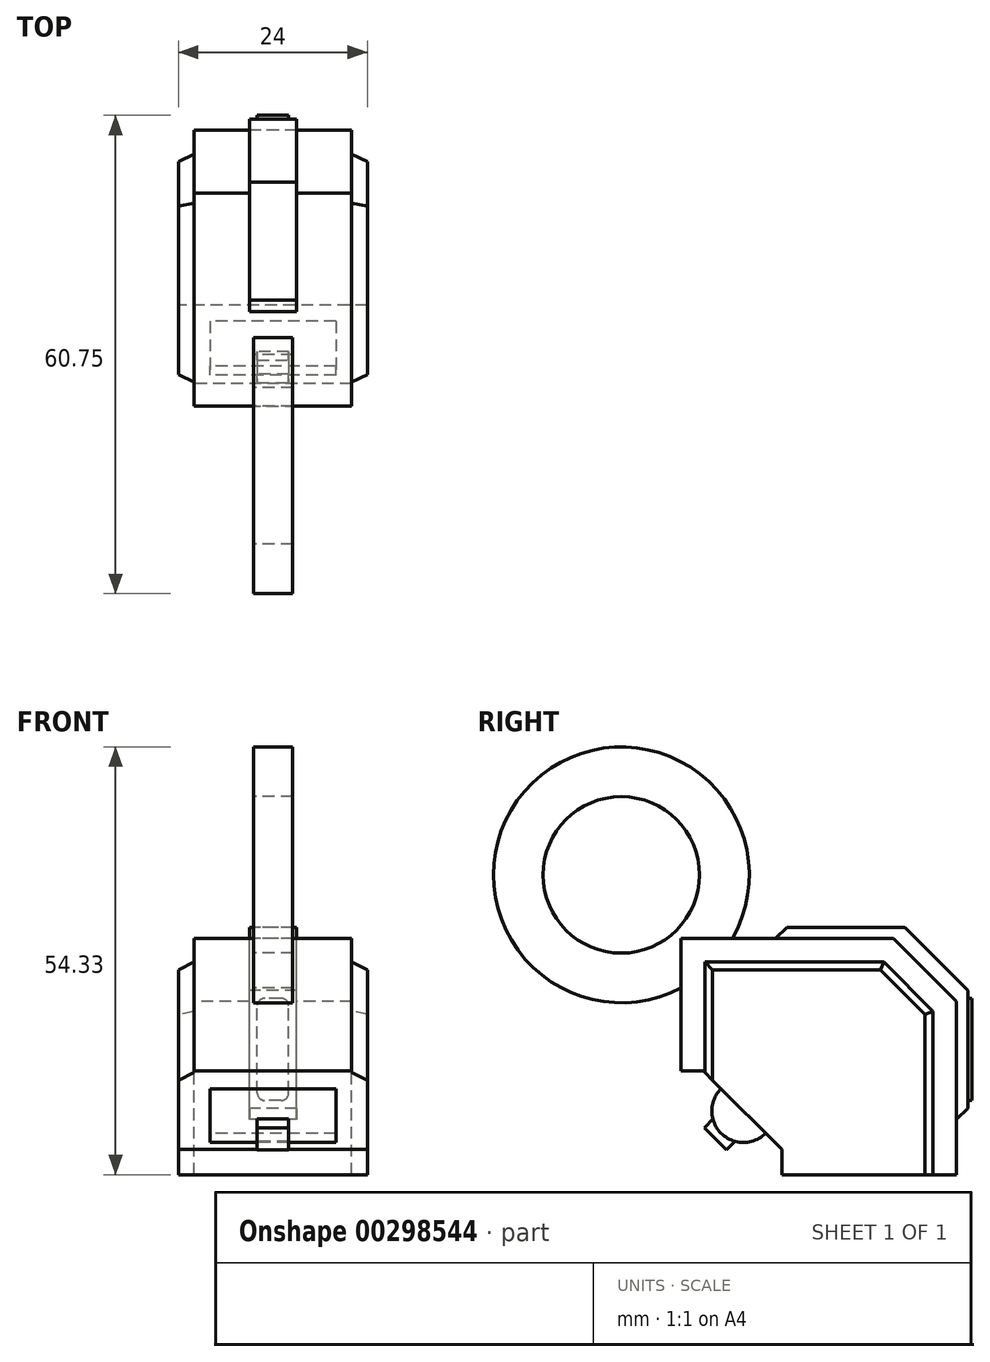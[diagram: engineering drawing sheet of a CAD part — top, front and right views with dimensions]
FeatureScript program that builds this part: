
annotation { "Feature Type Name" : "Feature", "Feature Type Description" : "" }
export const myFeature = defineFeature(function(context is Context, id is Id, definition is map)
    precondition{}
    {
        {
            var Q0;
            Q0=qCreatedBy(makeId("Right.planeOp"),FACE);
            cPlane(context, id + "F0", {"entities" : qUnion([Q0]), "cplaneType" : CPlaneType.OFFSET, "offset" : 10 * mm, "width" : 150 * mm, "height" : 150 * mm});
        }
        {
            var Q0;
            Q0=qCreatedBy(makeId("Right.planeOp"),FACE);
            var sketch = newSketch(context, id + "F1", { "sketchPlane" : qUnion([Q0])});
            skLineSegment(sketch, "E0.top", {"start": v(-35, 0) * mm, "end": v(0, 0) * mm});
            skLineSegment(sketch, "E0.left", {"start": v(-35, 30) * mm, "end": v(-35, 0) * mm});
            skLineSegment(sketch, "E1", {"start": v(0, 0) * mm, "end": v(0, 22) * mm});
            skLineSegment(sketch, "E2", {"start": v(-35, 30) * mm, "end": v(-8, 30) * mm});
            skLineSegment(sketch, "E3", {"start": v(-8, 30) * mm, "end": v(0, 22) * mm});
            skLineSegment(sketch, "E4.0", {"start": v(-32, 3) * mm, "end": v(-3, 3) * mm});
            skLineSegment(sketch, "E4.1", {"start": v(-32, 27) * mm, "end": v(-32, 3) * mm});
            skLineSegment(sketch, "E4.2", {"start": v(-3, 3) * mm, "end": v(-3, 20.76) * mm});
            skLineSegment(sketch, "E4.3", {"start": v(-9.24, 27) * mm, "end": v(-3, 20.76) * mm});
            skLineSegment(sketch, "E4.4", {"start": v(-32, 27) * mm, "end": v(-9.24, 27) * mm});
            skLineSegment(sketch, "E5.top", {"start": v(-3, 0) * mm, "end": v(-32, 0) * mm});
            skLineSegment(sketch, "E5.left", {"start": v(-3, 3) * mm, "end": v(-3, 0) * mm});
            skLineSegment(sketch, "E5.right", {"start": v(-32, 3) * mm, "end": v(-32, 0) * mm});
            skSolve(sketch);
        }
        {
            var Q0;
            Q0=makeQuery(id+"F1.imprint","IMPRINT",FACE,{"disambiguationData":[TD([[makeQuery(id+"F1.imprint","IMPRINT",EDGE,{"derivedFrom":sQuery(id+"F1.wireOp",EDGE,"E0.top")}),1.0]])]});
            extrude(context, id + "F2", {"entities" : qUnion([Q0]), "depth" : 20 * mm});
        }
        {
            var Q0;
            Q0=makeQuery(id+"F1.imprint","IMPRINT",FACE,{"disambiguationData":[TD([[makeQuery(id+"F1.imprint","IMPRINT",EDGE,{"derivedFrom":sQuery(id+"F1.wireOp",EDGE,"E4.0")}),1.0]])]});
            extrude(context, id + "F3", {"entities" : qUnion([Q0]), "operationType" : NewBodyOperationType.ADD, "depth" : 22 * mm, "hasSecondDirection" : true, "secondDirectionOppositeDirection" : true, "secondDirectionDepth" : 2 * mm});
        }
        {
            var Q0;
            Q0=makeQuery(id+"F2.opExtrude","SWEPT_FACE",FACE,{"disambiguationData":[OSD([sQuery(id+"F1.wireOp",EDGE,"E1")])]});
            var sketch = newSketch(context, id + "F4", { "sketchPlane" : qUnion([Q0])});
            skLineSegment(sketch, "E6", {"start": v(-13, 22) * mm, "end": v(-7, 22) * mm});
            skLineSegment(sketch, "E7.0", {"start": v(-13, 7) * mm, "end": v(-7, 7) * mm});
            skLineSegment(sketch, "E8", {"start": v(-13, 7) * mm, "end": v(-13, 22) * mm});
            skLineSegment(sketch, "E9", {"start": v(-7, 7) * mm, "end": v(-7, 22) * mm});
            skSolve(sketch);
        }
        {
            var Q0;
            Q0=makeQuery(id+"F2.opExtrude","SWEPT_FACE",FACE,{"disambiguationData":[OSD([sQuery(id+"F1.wireOp",EDGE,"E3")])]});
            var sketch = newSketch(context, id + "F5", { "sketchPlane" : qUnion([Q0])});
            skLineSegment(sketch, "E10.right", {"start": v(-13, 15.56) * mm, "end": v(-13, 26.87) * mm});
            skLineSegment(sketch, "E11.right", {"start": v(-7, 15.56) * mm, "end": v(-7, 26.87) * mm});
            skLineSegment(sketch, "E12", {"start": v(-13, 15.56) * mm, "end": v(-7, 15.56) * mm});
            skLineSegment(sketch, "E13", {"start": v(-13, 26.87) * mm, "end": v(-7, 26.87) * mm});
            skSolve(sketch);
        }
        {
            var Q0;
            Q0=makeQuery(id+"F2.opExtrude","SWEPT_FACE",FACE,{"disambiguationData":[OSD([sQuery(id+"F1.wireOp",EDGE,"E2")])]});
            var sketch = newSketch(context, id + "F6", { "sketchPlane" : qUnion([Q0])});
            skLineSegment(sketch, "E14", {"start": v(7, -8) * mm, "end": v(13, -8) * mm});
            skLineSegment(sketch, "E15.0", {"start": v(13, -23) * mm, "end": v(7, -23) * mm});
            skLineSegment(sketch, "E16", {"start": v(7, -23) * mm, "end": v(7, -8) * mm});
            skLineSegment(sketch, "E17", {"start": v(13, -23) * mm, "end": v(13, -8) * mm});
            skSolve(sketch);
        }
        {
            var Q0;
            Q0=makeQuery(id+"F1.imprint","IMPRINT",FACE,{"disambiguationData":[TD([[makeQuery(id+"F1.imprint","IMPRINT",EDGE,{"derivedFrom":sQuery(id+"F1.wireOp",EDGE,"E4.0")}),-1.0]])]});
            extrude(context, id + "F7", {"entities" : qUnion([Q0]), "operationType" : NewBodyOperationType.ADD, "depth" : 22 * mm, "hasSecondDirection" : true, "secondDirectionOppositeDirection" : true, "secondDirectionDepth" : 2 * mm});
        }
        {
            var Q0;
            Q0=makeQuery(id+"F5.imprint","IMPRINT",FACE,{"disambiguationData":[TD([[makeQuery(id+"F5.imprint","IMPRINT",EDGE,{"derivedFrom":sQuery(id+"F5.wireOp",EDGE,"E10.right")}),-1.0]])]});
            var Q1;
            Q1=makeQuery(id+"F4.imprint","IMPRINT",FACE,{"disambiguationData":[TD([[makeQuery(id+"F4.imprint","IMPRINT",EDGE,{"derivedFrom":sQuery(id+"F4.wireOp",EDGE,"E6")}),-1.0]])]});
            var Q2;
            Q2=makeQuery(id+"F6.imprint","IMPRINT",FACE,{"disambiguationData":[TD([[makeQuery(id+"F6.imprint","IMPRINT",EDGE,{"derivedFrom":sQuery(id+"F6.wireOp",EDGE,"E14")}),1.0]])]});
            extrude(context, id + "F8", {"entities" : qUnion([Q0, Q1, Q2]), "operationType" : NewBodyOperationType.ADD, "depth" : 2 * mm});
        }
        {
            var Q0;
            Q0=makeQuery(id+"F3.opExtrude","CAP_FACE",FACE,{"disambiguationData":[OSD([sQuery(id+"F1.wireOp",EDGE,"E4.0"),sQuery(id+"F1.wireOp",EDGE,"E4.1"),sQuery(id+"F1.wireOp",EDGE,"E4.2"),sQuery(id+"F1.wireOp",EDGE,"E4.3"),sQuery(id+"F1.wireOp",EDGE,"E4.4")])],"isStart":true});
            var sketch = newSketch(context, id + "F9", { "sketchPlane" : qUnion([Q0])});
            skLineSegment(sketch, "E18.bottom", {"start": v(42.19, -6.81) * mm, "end": v(22.19, -6.81) * mm});
            skLineSegment(sketch, "E18.top", {"start": v(42.19, 13.19) * mm, "end": v(32.19, 13.19) * mm});
            skLineSegment(sketch, "E18.left", {"start": v(42.19, -6.81) * mm, "end": v(42.19, 13.19) * mm});
            skLineSegment(sketch, "E18.right", {"start": v(22.19, -6.81) * mm, "end": v(22.19, 3.19) * mm});
            skLineSegment(sketch, "E19", {"start": v(32.19, 13.19) * mm, "end": v(22.19, 3.19) * mm});
            skSolve(sketch);
        }
        {
            var Q0;
            {var subQ1=sQuery(id+"F9.wireOp",EDGE,"E18.bottom");Q0=makeQuery(id+"F9.imprint","IMPRINT",FACE,{"disambiguationData":[TD([[makeQuery(id+"F9.imprint","IMPRINT",EDGE,{"derivedFrom":subQ1}),-1.0]])]});}
            var Q1;
            {var subQ0=sQuery(id+"F9.wireOp",EDGE,"E19");var subQ1=sQuery(id+"F9.wireOp",EDGE,"E18.right");var subQ2=makeQuery(id+"F9.imprint","INTERSECT",VERTEX,{"derivedFrom":[subQ1,subQ0]});Q1=makeQuery(id+"F9.imprint","IMPRINT",FACE,{"disambiguationData":[TD([[makeQuery(id+"F9.imprint","IMPRINT",EDGE,{"disambiguationData":[TD([[subQ2,1.0]])],"derivedFrom":subQ1}),-1.0]])]});}
            extrude(context, id + "F10", {"entities" : qUnion([Q0, Q1]), "operationType" : NewBodyOperationType.REMOVE, "oppositeDirection" : true, "depth" : 25 * mm});
        }
        {
            var Q0;
            Q0=makeQuery(id+"F10.boolean.opBoolean","COPY",FACE,{"derivedFrom":makeQuery(id+"F10.opExtrude","SWEPT_FACE",FACE,{"disambiguationData":[OSD([sQuery(id+"F9.wireOp",EDGE,"E19")])]})});
            var sketch = newSketch(context, id + "F11", { "sketchPlane" : qUnion([Q0])});
            skLineSegment(sketch, "E20.bottom", {"start": v(2, 24.88) * mm, "end": v(8, 24.88) * mm});
            skLineSegment(sketch, "E20.top", {"start": v(2, 28.88) * mm, "end": v(18, 28.88) * mm});
            skLineSegment(sketch, "E21.0", {"start": v(2, 24.88) * mm, "end": v(2, 28.88) * mm});
            skLineSegment(sketch, "E22.0", {"start": v(18, 24.88) * mm, "end": v(18, 28.88) * mm});
            skLineSegment(sketch, "E23.trimOffspring", {"start": v(12, 24.88) * mm, "end": v(18, 24.88) * mm});
            skLineSegment(sketch, "E24", {"start": v(8, 22.88) * mm, "end": v(12, 22.88) * mm});
            skLineSegment(sketch, "E25", {"start": v(8, 26.88) * mm, "end": v(12, 26.88) * mm});
            skLineSegment(sketch, "E26", {"start": v(8, 22.88) * mm, "end": v(8, 26.88) * mm});
            skLineSegment(sketch, "E27", {"start": v(12, 22.88) * mm, "end": v(12, 26.88) * mm});
            skSolve(sketch);
        }
        {
            var Q0;
            {var subQ3=sQuery(id+"F11.wireOp",EDGE,"E24");Q0=makeQuery(id+"F11.imprint","IMPRINT",FACE,{"disambiguationData":[TD([[makeQuery(id+"F11.imprint","IMPRINT",EDGE,{"derivedFrom":subQ3}),1.0]])]});}
            extrude(context, id + "F12", {"entities" : qUnion([Q0]), "operationType" : NewBodyOperationType.ADD, "depth" : 5 * mm});
        }
        {
            var Q0;
            {var subQ0=sQuery(id+"F11.wireOp",EDGE,"E20.bottom");Q0=makeQuery(id+"F11.imprint","IMPRINT",FACE,{"disambiguationData":[TD([[makeQuery(id+"F11.imprint","IMPRINT",EDGE,{"derivedFrom":subQ0}),1.0]])]});}
            var Q1;
            Q1=sQuery(id+"F11.wireOp",EDGE,"E20.bottom");
            revolve(context, id + "F13", {"operationType" : NewBodyOperationType.ADD, "entities" : qUnion([Q0]), "axis" : qUnion([Q1]), "revolveType" : RevolveType.FULL});
        }
        {
            var Q0;
            Q0=makeQuery(id+"F8.opExtrude","CAP_FACE",FACE,{"disambiguationData":[OSD([sQuery(id+"F4.wireOp",EDGE,"E6"),sQuery(id+"F4.wireOp",EDGE,"E7.0"),sQuery(id+"F4.wireOp",EDGE,"E8"),sQuery(id+"F4.wireOp",EDGE,"E9")]),OD(1.0)],"isStart":false});
            var sketch = newSketch(context, id + "F14", { "sketchPlane" : qUnion([Q0])});
            skLineSegment(sketch, "E28.0", {"start": v(-12, 10.41) * mm, "end": v(-12, 21.41) * mm});
            skLineSegment(sketch, "E28.1", {"start": v(-11, 9.41) * mm, "end": v(-9, 9.41) * mm});
            skLineSegment(sketch, "E28.2", {"start": v(-8, 10.41) * mm, "end": v(-8, 21.41) * mm});
            skLineSegment(sketch, "E28.3", {"start": v(-11, 22.41) * mm, "end": v(-9, 22.41) * mm});
            skPoint(sketch, "E29.visualSharp", {"position": v(-8, 22.41) * mm});
            skArc(sketch, "E29.filletArc", {"start": v(-8, 21.41) * mm, "mid": v(-8.3, 22.12) * mm, "end": v(-9, 22.41) * mm});
            skPoint(sketch, "E30.visualSharp", {"position": v(-12, 22.41) * mm});
            skArc(sketch, "E30.filletArc", {"start": v(-11, 22.41) * mm, "mid": v(-11.7, 22.12) * mm, "end": v(-12, 21.41) * mm});
            skPoint(sketch, "E31.visualSharp", {"position": v(-8, 9.41) * mm});
            skArc(sketch, "E31.filletArc", {"start": v(-9, 9.41) * mm, "mid": v(-8.3, 9.7) * mm, "end": v(-8, 10.41) * mm});
            skPoint(sketch, "E32.visualSharp", {"position": v(-12, 9.41) * mm});
            skArc(sketch, "E32.filletArc", {"start": v(-12, 10.41) * mm, "mid": v(-11.7, 9.7) * mm, "end": v(-11, 9.41) * mm});
            skSolve(sketch);
        }
        {
            var Q0;
            Q0=makeQuery(id+"F14.imprint","IMPRINT",FACE,{"disambiguationData":[TD([[makeQuery(id+"F14.imprint","IMPRINT",EDGE,{"derivedFrom":sQuery(id+"F14.wireOp",EDGE,"E28.0")}),-1.0]])]});
            extrude(context, id + "F15", {"entities" : qUnion([Q0]), "operationType" : NewBodyOperationType.ADD, "depth" : 0.5 * mm});
        }
        {
            var Q0;
            Q0=qCreatedBy(id+"F0.planeOp",FACE);
            var sketch = newSketch(context, id + "F16", { "sketchPlane" : qUnion([Q0])});
            skCircle(sketch, "E33", {"center": v(-42.59, 38.08) * mm, "radius": 16.25 * mm});
            skCircle(sketch, "E34", {"center": v(-42.59, 38.08) * mm, "radius": 9.94 * mm});
            skSolve(sketch);
        }
        {
            var Q0;
            Q0=makeQuery(id+"F16.imprint","IMPRINT",FACE,{"disambiguationData":[TD([[makeQuery(id+"F16.imprint","IMPRINT",EDGE,{"derivedFrom":sQuery(id+"F16.wireOp",EDGE,"E33")}),1.0]])]});
            extrude(context, id + "F17", {"entities" : qUnion([Q0]), "operationType" : NewBodyOperationType.ADD, "depth" : 2.5 * mm, "hasSecondDirection" : true, "secondDirectionOppositeDirection" : true, "secondDirectionDepth" : 2.5 * mm});
        }
        {
            var Q0;
            Q0=makeQuery(id+"F7.boolean.opBoolean","MERGE",EDGE,{"derivedFrom":[makeQuery(id+"F3.opExtrude","CAP_EDGE",EDGE,{"disambiguationData":[OSD([sQuery(id+"F1.wireOp",EDGE,"E4.2")])],"isStart":true}),makeQuery(id+"F7.opExtrude","CAP_EDGE",EDGE,{"disambiguationData":[OSD([sQuery(id+"F1.wireOp",EDGE,"E5.left")])],"isStart":true})]});
            var Q1;
            Q1=makeQuery(id+"F3.opExtrude","CAP_EDGE",EDGE,{"disambiguationData":[OSD([sQuery(id+"F1.wireOp",EDGE,"E4.3")])],"isStart":true});
            var Q2;
            Q2=makeQuery(id+"F3.opExtrude","CAP_EDGE",EDGE,{"disambiguationData":[OSD([sQuery(id+"F1.wireOp",EDGE,"E4.4")])],"isStart":true});
            var Q3;
            Q3=makeQuery(id+"F7.boolean.opBoolean","MERGE",EDGE,{"derivedFrom":[makeQuery(id+"F3.opExtrude","CAP_EDGE",EDGE,{"disambiguationData":[OSD([sQuery(id+"F1.wireOp",EDGE,"E4.1")])],"isStart":true}),makeQuery(id+"F7.opExtrude","CAP_EDGE",EDGE,{"disambiguationData":[OSD([sQuery(id+"F1.wireOp",EDGE,"E5.right")])],"isStart":true})]});
            chamfer(context, id + "F18", {"entities" : qUnion([Q0, Q1, Q2, Q3]), "chamferType" : ChamferType.TWO_OFFSETS, "width1" : 2 * mm, "oppositeDirection" : false, "width2" : 1 * mm, "tangentPropagation" : true});
        }
        {
            var Q0;
            Q0=makeQuery(id+"F7.boolean.opBoolean","MERGE",EDGE,{"derivedFrom":[makeQuery(id+"F3.opExtrude","CAP_EDGE",EDGE,{"disambiguationData":[OSD([sQuery(id+"F1.wireOp",EDGE,"E4.2")])],"isStart":false}),makeQuery(id+"F7.opExtrude","CAP_EDGE",EDGE,{"disambiguationData":[OSD([sQuery(id+"F1.wireOp",EDGE,"E5.left")])],"isStart":false})]});
            var Q1;
            Q1=makeQuery(id+"F3.opExtrude","CAP_EDGE",EDGE,{"disambiguationData":[OSD([sQuery(id+"F1.wireOp",EDGE,"E4.3")])],"isStart":false});
            var Q2;
            Q2=makeQuery(id+"F3.opExtrude","CAP_EDGE",EDGE,{"disambiguationData":[OSD([sQuery(id+"F1.wireOp",EDGE,"E4.4")])],"isStart":false});
            var Q3;
            Q3=makeQuery(id+"F7.boolean.opBoolean","MERGE",EDGE,{"derivedFrom":[makeQuery(id+"F3.opExtrude","CAP_EDGE",EDGE,{"disambiguationData":[OSD([sQuery(id+"F1.wireOp",EDGE,"E4.1")])],"isStart":false}),makeQuery(id+"F7.opExtrude","CAP_EDGE",EDGE,{"disambiguationData":[OSD([sQuery(id+"F1.wireOp",EDGE,"E5.right")])],"isStart":false})]});
            chamfer(context, id + "F19", {"entities" : qUnion([Q0, Q1, Q2, Q3]), "chamferType" : ChamferType.TWO_OFFSETS, "width1" : 1 * mm, "oppositeDirection" : false, "width2" : 2 * mm, "tangentPropagation" : true});
        }
    });
